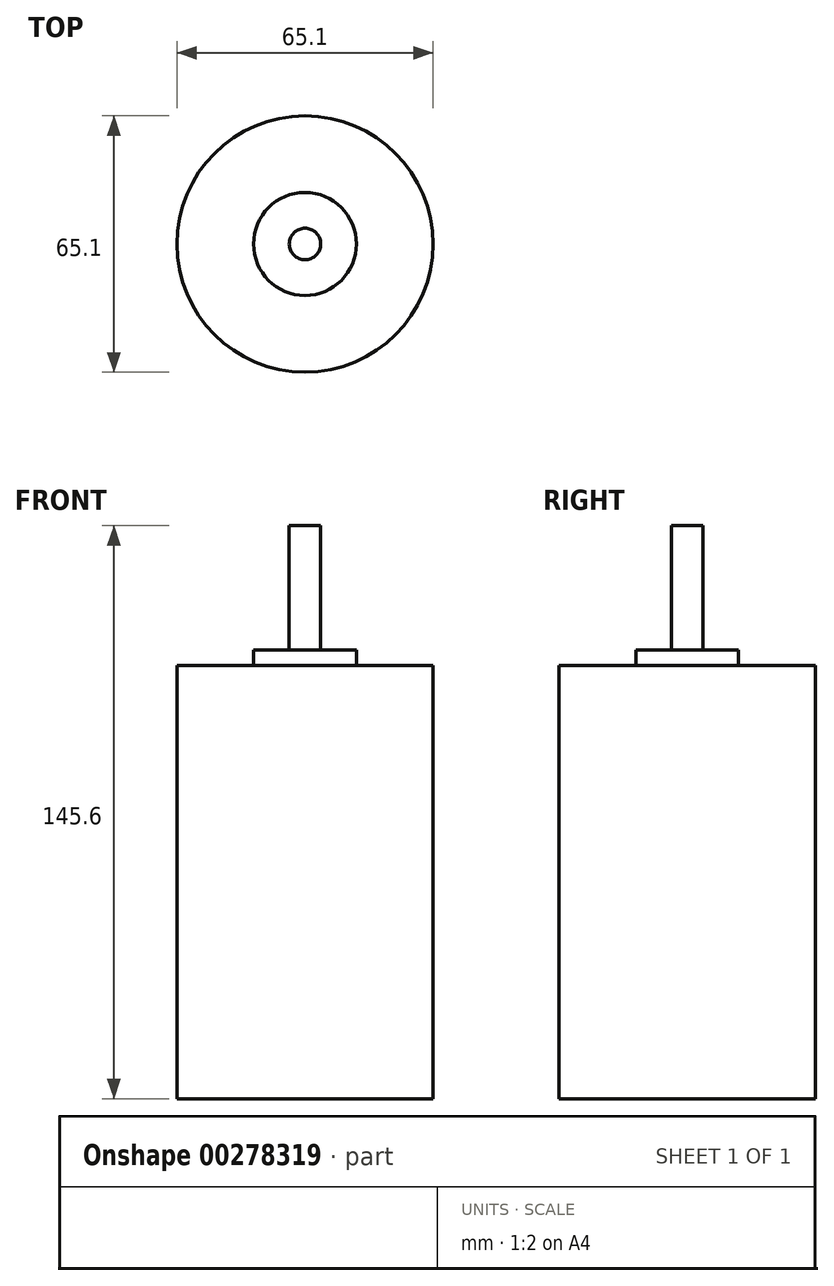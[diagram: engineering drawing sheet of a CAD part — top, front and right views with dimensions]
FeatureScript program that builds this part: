
annotation { "Feature Type Name" : "Feature", "Feature Type Description" : "" }
export const myFeature = defineFeature(function(context is Context, id is Id, definition is map)
    precondition{}
    {
        {
            var Q0;
            Q0=qCreatedBy(makeId("Top.planeOp"),FACE);
            var sketch = newSketch(context, id + "F0", { "sketchPlane" : qUnion([Q0])});
            skCircle(sketch, "E0", {"center": v(0, 0) * mm, "radius": 32.55 * mm});
            skSolve(sketch);
        }
        {
            var Q0;
            Q0=makeQuery(id+"F0.imprint","IMPRINT",FACE,{"disambiguationData":[TD([[makeQuery(id+"F0.imprint","IMPRINT",EDGE,{"derivedFrom":sQuery(id+"F0.wireOp",EDGE,"E0")}),1.0]])]});
            extrude(context, id + "F1", {"entities" : qUnion([Q0]), "depth" : 110 * mm});
        }
        {
            var Q0;
            Q0=makeQuery(id+"F1.opExtrude","CAP_FACE",FACE,{"disambiguationData":[OSD([sQuery(id+"F0.wireOp",EDGE,"E0")])],"isStart":false});
            var sketch = newSketch(context, id + "F2", { "sketchPlane" : qUnion([Q0])});
            skCircle(sketch, "E1", {"center": v(0, 0) * mm, "radius": 13.07 * mm});
            skSolve(sketch);
        }
        {
            var Q0;
            Q0=makeQuery(id+"F2.imprint","IMPRINT",FACE,{"disambiguationData":[TD([[makeQuery(id+"F2.imprint","IMPRINT",EDGE,{"derivedFrom":sQuery(id+"F2.wireOp",EDGE,"E1")}),1.0]])]});
            extrude(context, id + "F3", {"entities" : qUnion([Q0]), "operationType" : NewBodyOperationType.ADD, "depth" : 4 * mm});
        }
        {
            var Q0;
            Q0=makeQuery(id+"F1.opExtrude","CAP_FACE",FACE,{"disambiguationData":[OSD([sQuery(id+"F0.wireOp",EDGE,"E0")])],"isStart":false});
            var sketch = newSketch(context, id + "F4", { "sketchPlane" : qUnion([Q0])});
            skCircle(sketch, "E2", {"center": v(0, 0) * mm, "radius": 4 * mm});
            skSolve(sketch);
        }
        {
            var Q0;
            Q0 = qSketchRegion(id + "F4", true);
            extrude(context, id + "F5", {"entities" : qUnion([Q0]), "operationType" : NewBodyOperationType.ADD, "depth" : 35.6 * mm});
        }
    });
